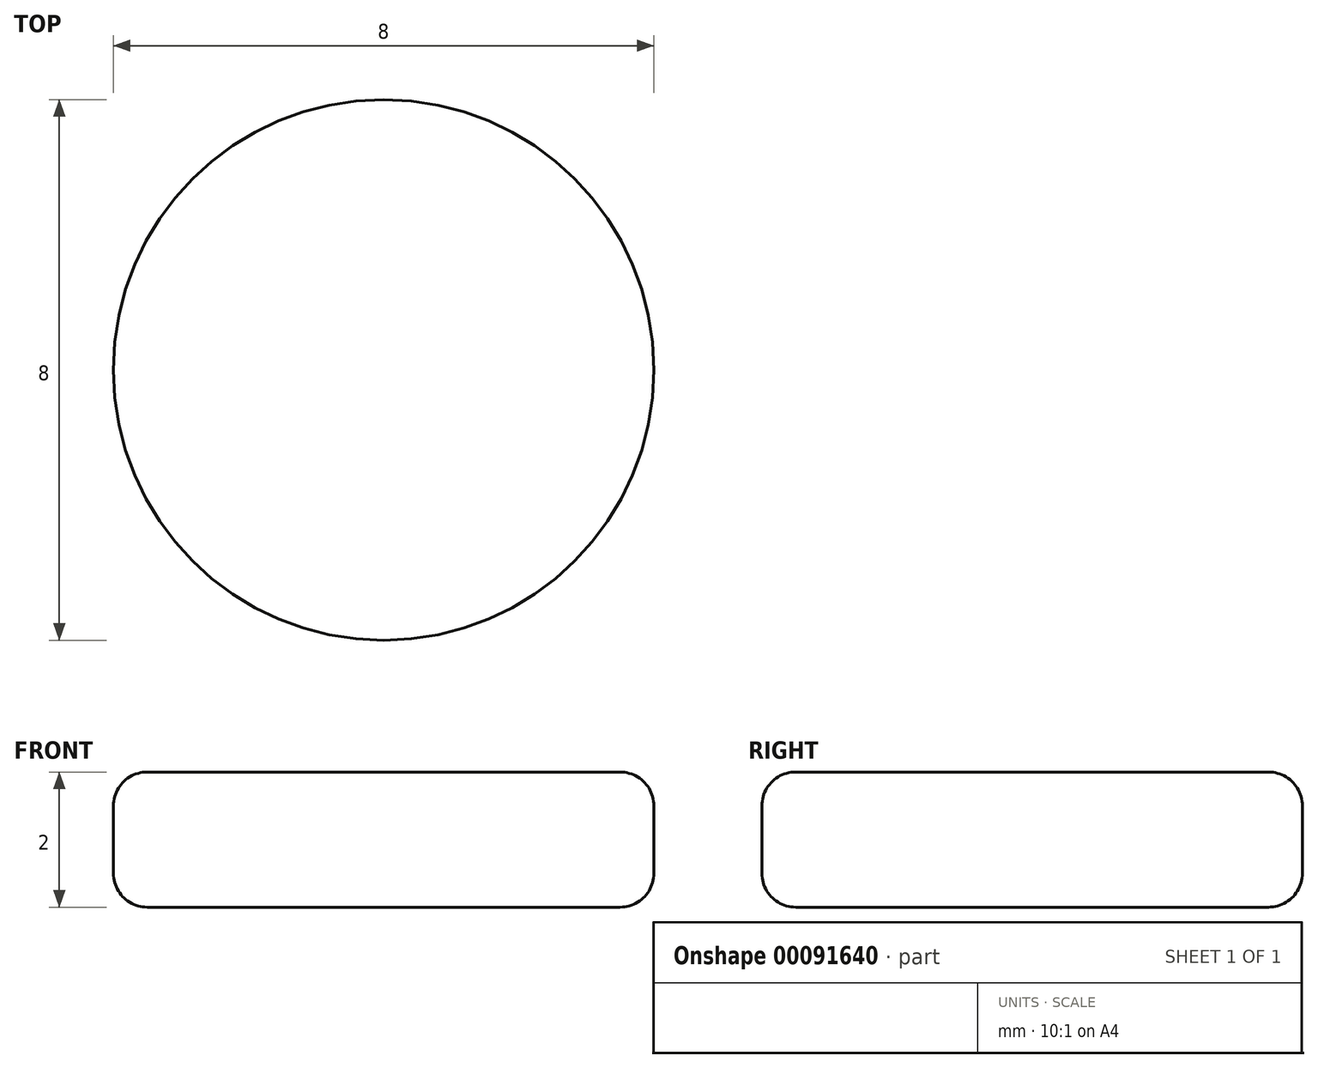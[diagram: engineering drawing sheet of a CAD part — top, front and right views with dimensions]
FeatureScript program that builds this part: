
annotation { "Feature Type Name" : "Feature", "Feature Type Description" : "" }
export const myFeature = defineFeature(function(context is Context, id is Id, definition is map)
    precondition{}
    {
        {
            var Q0;
            Q0=qCreatedBy(makeId("Top.planeOp"),FACE);
            var sketch = newSketch(context, id + "F0", { "sketchPlane" : qUnion([Q0])});
            skCircle(sketch, "E0", {"center": v(0, 0) * mm, "radius": 4 * mm});
            skSolve(sketch);
        }
        {
            var Q0;
            Q0 = qSketchRegion(id + "F0", true);
            extrude(context, id + "F1", {"entities" : qUnion([Q0]), "depth" : 2 * mm});
        }
        {
            var Q0;
            Q0=makeQuery(id+"F1.opExtrude","CAP_EDGE",EDGE,{"disambiguationData":[OSD([sQuery(id+"F0.wireOp",EDGE,"E0")])],"isStart":false});
            var Q1;
            Q1=makeQuery(id+"F1.opExtrude","CAP_EDGE",EDGE,{"disambiguationData":[OSD([sQuery(id+"F0.wireOp",EDGE,"E0")])],"isStart":true});
            fillet(context, id + "F2", {"entities" : qUnion([Q0, Q1]), "radius" : .5 * mm, "tangentPropagation" : true, "allowEdgeOverflow" : false});
        }
    });
